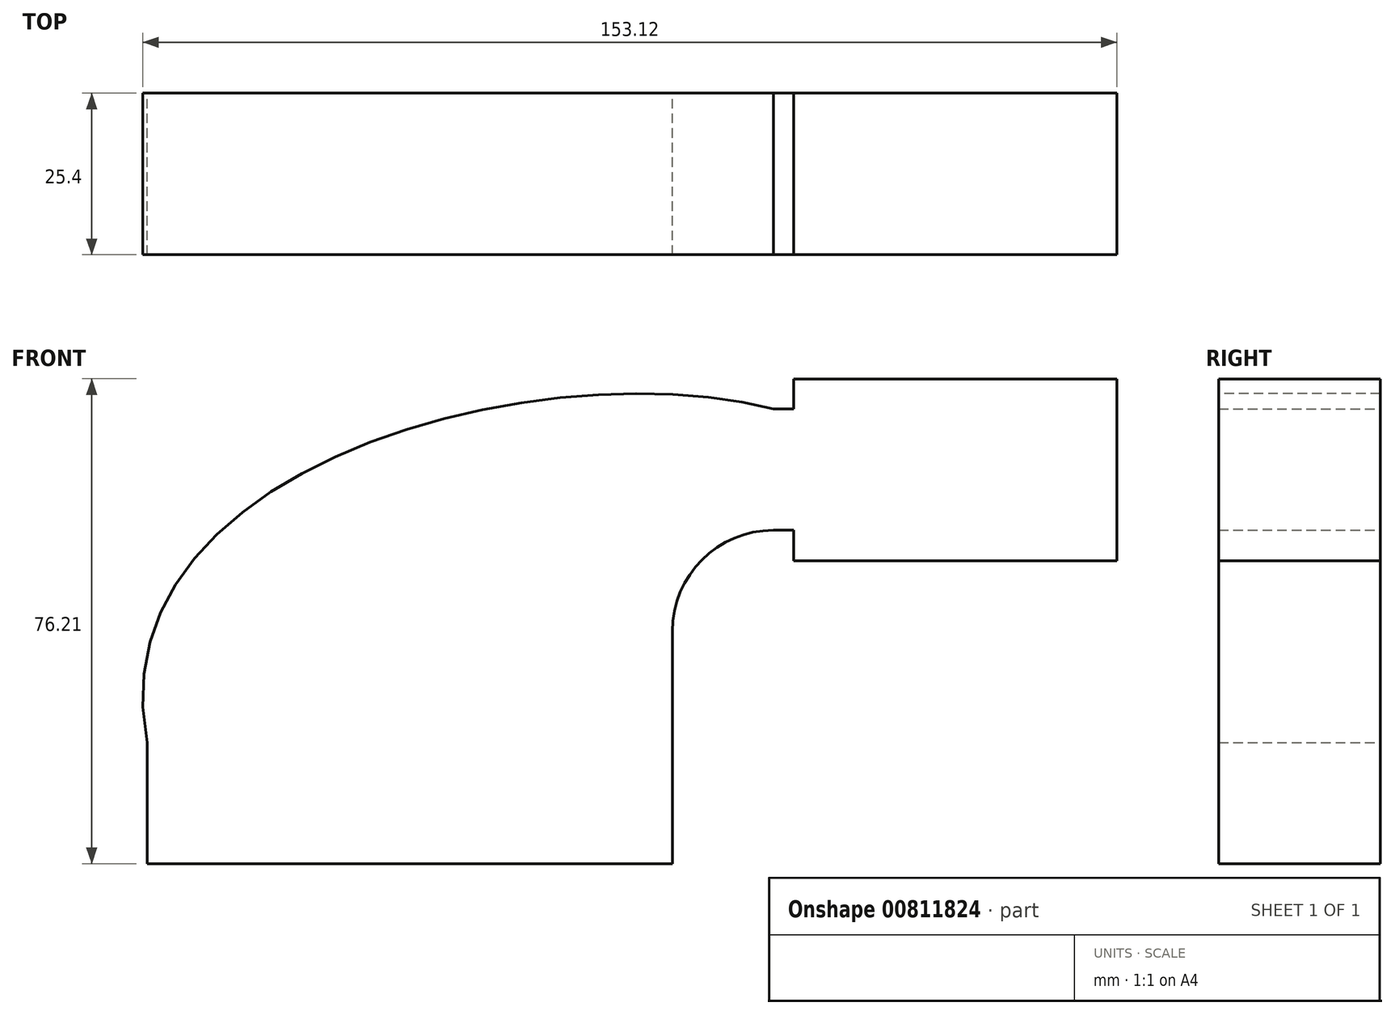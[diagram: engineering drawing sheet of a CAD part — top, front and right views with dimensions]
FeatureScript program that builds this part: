
annotation { "Feature Type Name" : "Feature", "Feature Type Description" : "" }
export const myFeature = defineFeature(function(context is Context, id is Id, definition is map)
    precondition{}
    {
        {
            var Q0;
            Q0=qCreatedBy(makeId("Front.planeOp"),FACE);
            var sketch = newSketch(context, id + "F0", { "sketchPlane" : qUnion([Q0])});
            skLineSegment(sketch, "E0.bottom", {"start": v(-41.28, 9.52) * mm, "end": v(41.27, 9.53) * mm});
            skLineSegment(sketch, "E0.top", {"start": v(-41.28, -9.53) * mm, "end": v(41.28, -9.53) * mm});
            skLineSegment(sketch, "E0.left", {"start": v(-41.28, 9.52) * mm, "end": v(-41.28, -9.53) * mm});
            skLineSegment(sketch, "E0.right", {"start": v(41.27, 9.53) * mm, "end": v(41.28, -9.52) * mm});
            skPoint(sketch, "E0.middle", {"position": v(0, 0) * mm});
            skLineSegment(sketch, "E1.bottom", {"start": v(111.13, 38.1) * mm, "end": v(60.33, 38.1) * mm});
            skLineSegment(sketch, "E1.top", {"start": v(111.13, 66.68) * mm, "end": v(60.33, 66.68) * mm});
            skLineSegment(sketch, "E1.left", {"start": v(111.13, 38.1) * mm, "end": v(111.13, 66.68) * mm});
            skLineSegment(sketch, "E1.right", {"start": v(60.33, 38.1) * mm, "end": v(60.33, 66.68) * mm});
            skPoint(sketch, "E1.middle", {"position": v(85.73, 52.39) * mm});
            skLineSegment(sketch, "E2", {"start": v(41.27, 9.53) * mm, "end": v(41.27, 27) * mm});
            skPoint(sketch, "E3.endSnap0", {"position": v(41.27, 18.26) * mm});
            skArc(sketch, "E4", {"start": v(41.27, 27) * mm, "mid": v(45.92, 38.23) * mm, "end": v(57.15, 42.88) * mm});
            skLineSegment(sketch, "E5", {"start": v(57.15, 42.88) * mm, "end": v(84.89, 42.88) * mm});
            skLineSegment(sketch, "E6.0", {"start": v(57.15, 61.93) * mm, "end": v(84.89, 61.93) * mm});
            skArc(sketch, "E6.1", {"start": v(22.22, 27) * mm, "mid": v(32.45, 51.7) * mm, "end": v(57.15, 61.93) * mm});
            skLineSegment(sketch, "E6.2", {"start": v(22.22, 9.53) * mm, "end": v(22.22, 27) * mm});
            skFitSpline(sketch, "E7", {"points": [v(-41.28, 9.52) * mm, v(57.15, 61.93) * mm], "startDerivative": vector(-25.67, 130.76) * mm, "endDerivative": vector(109.72, -28.3) * mm});
            skSolve(sketch);
        }
        {
            var Q0;
            Q0 = qSketchRegion(id + "F0", true);
            extrude(context, id + "F1", {"entities" : qUnion([Q0]), "depth" : 25.4 * mm, "offsetDistance" : 25.4 * mm});
        }
    });
